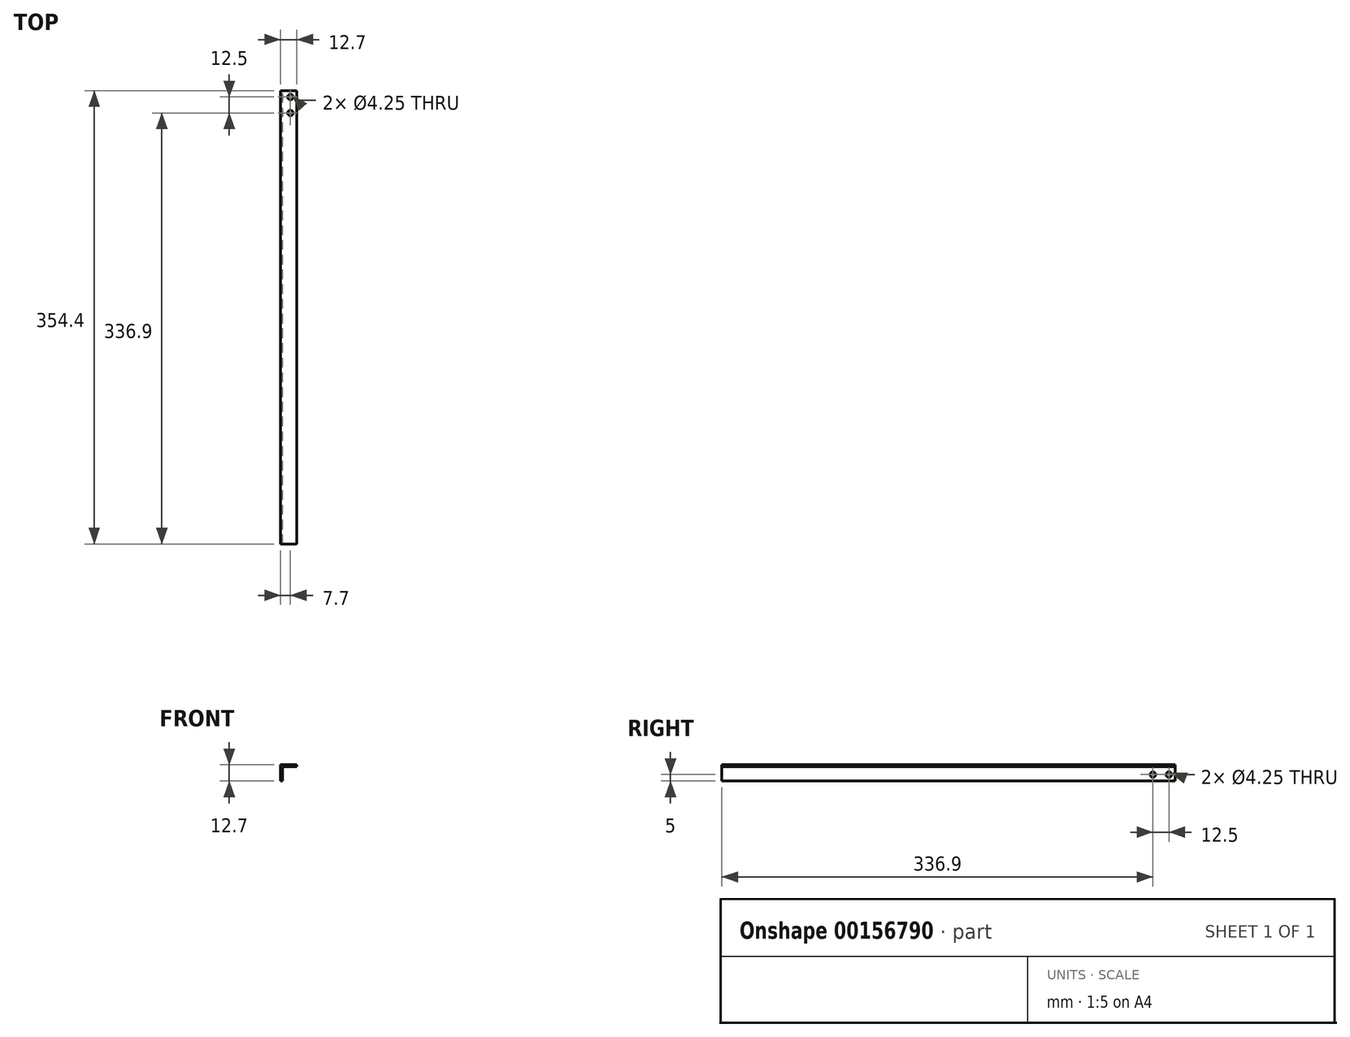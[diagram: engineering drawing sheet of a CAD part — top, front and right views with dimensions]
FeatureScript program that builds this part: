
annotation { "Feature Type Name" : "Feature", "Feature Type Description" : "" }
export const myFeature = defineFeature(function(context is Context, id is Id, definition is map)
    precondition{}
    {
        {
            var Q0;
            Q0=qCreatedBy(makeId("Front.planeOp"),FACE);
            var sketch = newSketch(context, id + "F0", { "sketchPlane" : qUnion([Q0])});
            skLineSegment(sketch, "E0", {"start": v(12.7, 0) * mm, "end": v(0, 0) * mm});
            skLineSegment(sketch, "E1", {"start": v(0, 0) * mm, "end": v(0, -12.7) * mm});
            skLineSegment(sketch, "E2", {"start": v(0, -12.7) * mm, "end": v(1.6, -12.7) * mm});
            skLineSegment(sketch, "E3", {"start": v(1.6, -12.7) * mm, "end": v(1.6, -1.6) * mm});
            skLineSegment(sketch, "E4", {"start": v(1.6, -1.6) * mm, "end": v(12.7, -1.6) * mm});
            skLineSegment(sketch, "E5", {"start": v(12.7, -1.6) * mm, "end": v(12.7, 0) * mm});
            skLineSegment(sketch, "E6", {"start": v(12.7, -1.6) * mm, "end": v(1.6, -12.7) * mm, "construction": true});
            skLineSegment(sketch, "E7", {"start": v(0, -12.7) * mm, "end": v(12.7, 0) * mm, "construction": true});
            skSolve(sketch);
        }
        {
            var Q0;
            Q0 = qSketchRegion(id + "F0", true);
            extrude(context, id + "F1", {"entities" : qUnion([Q0]), "endBound" : BoundingType.SYMMETRIC, "depth" : 354.4 * mm});
        }
        {
            var Q0;
            Q0=makeQuery(id+"F1.opExtrude","SWEPT_FACE",FACE,{"disambiguationData":[OSD([sQuery(id+"F0.wireOp",EDGE,"E0")])]});
            var sketch = newSketch(context, id + "F2", { "sketchPlane" : qUnion([Q0])});
            skCircle(sketch, "E8", {"center": v(7.7, 172.2) * mm, "radius": 2.12 * mm});
            skCircle(sketch, "E9", {"center": v(7.7, 159.7) * mm, "radius": 2.12 * mm});
            skSolve(sketch);
        }
        {
            var Q0;
            Q0 = qSketchRegion(id + "F2", true);
            extrude(context, id + "F3", {"entities" : qUnion([Q0]), "operationType" : NewBodyOperationType.REMOVE, "oppositeDirection" : true, "depth" : 5 * mm});
        }
        {
            var Q0;
            Q0=makeQuery(id+"F1.opExtrude","SWEPT_FACE",FACE,{"disambiguationData":[OSD([sQuery(id+"F0.wireOp",EDGE,"E3")])]});
            var sketch = newSketch(context, id + "F4", { "sketchPlane" : qUnion([Q0])});
            skCircle(sketch, "E10", {"center": v(172.2, -7.7) * mm, "radius": 2.12 * mm});
            skCircle(sketch, "E11", {"center": v(159.7, -7.7) * mm, "radius": 2.12 * mm});
            skSolve(sketch);
        }
        {
            var Q0;
            Q0 = qSketchRegion(id + "F4", true);
            extrude(context, id + "F5", {"entities" : qUnion([Q0]), "operationType" : NewBodyOperationType.REMOVE, "oppositeDirection" : true, "depth" : 5 * mm});
        }
    });
